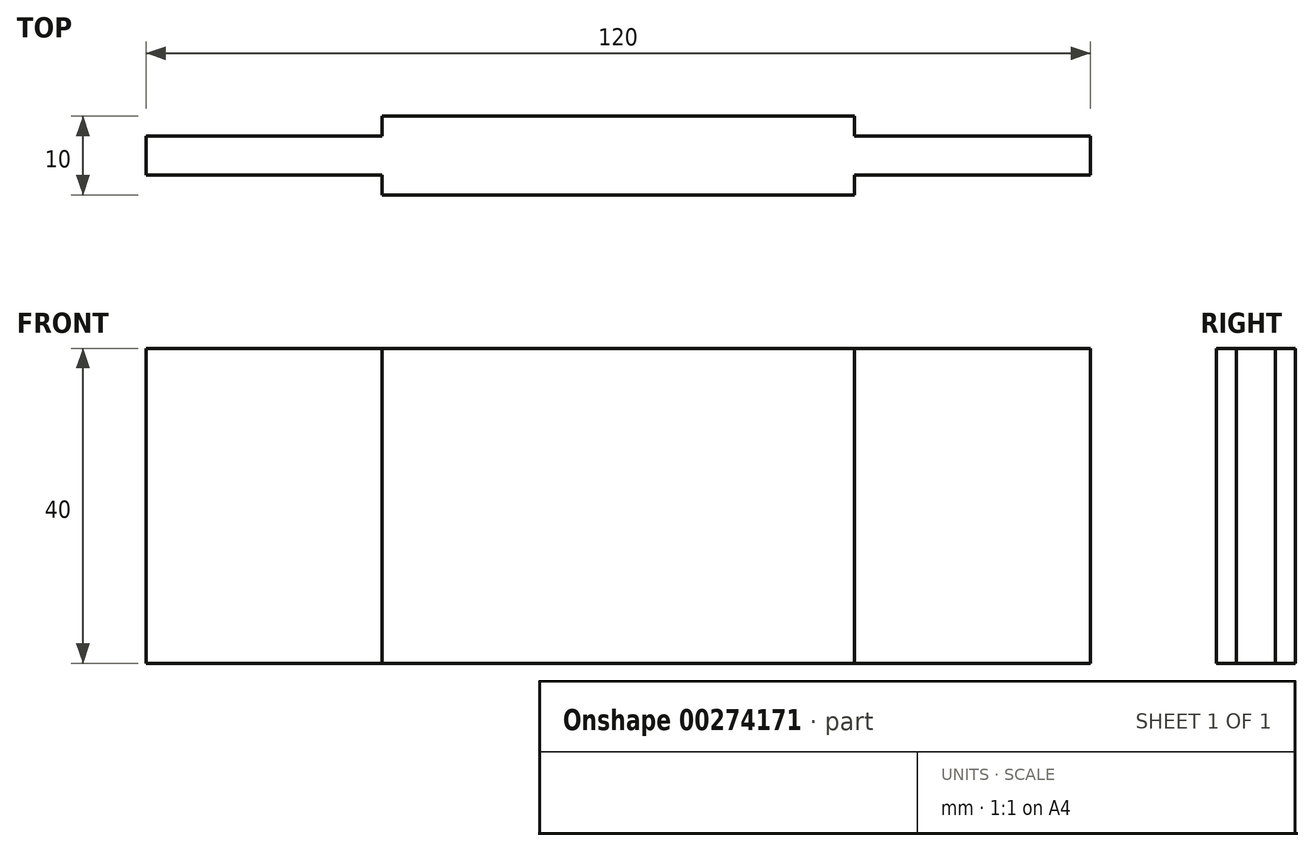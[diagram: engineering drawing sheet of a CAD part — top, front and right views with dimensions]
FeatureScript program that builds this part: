
annotation { "Feature Type Name" : "Feature", "Feature Type Description" : "" }
export const myFeature = defineFeature(function(context is Context, id is Id, definition is map)
    precondition{}
    {
        {
            var Q0;
            Q0=qCreatedBy(makeId("Top.planeOp"),FACE);
            var sketch = newSketch(context, id + "F0", { "sketchPlane" : qUnion([Q0])});
            skLineSegment(sketch, "E0.bottom", {"start": v(60, -5) * mm, "end": v(-60, -5) * mm});
            skLineSegment(sketch, "E0.top", {"start": v(60, 5) * mm, "end": v(-60, 5) * mm});
            skLineSegment(sketch, "E0.left", {"start": v(60, -5) * mm, "end": v(60, 5) * mm});
            skLineSegment(sketch, "E0.right", {"start": v(-60, -5) * mm, "end": v(-60, 5) * mm});
            skPoint(sketch, "E0.middle", {"position": v(0, 0) * mm});
            skLineSegment(sketch, "E1.bottom", {"start": v(-60, 5) * mm, "end": v(-30, 5) * mm});
            skLineSegment(sketch, "E1.top", {"start": v(-60, 2.5) * mm, "end": v(-30, 2.5) * mm});
            skLineSegment(sketch, "E1.left", {"start": v(-60, 5) * mm, "end": v(-60, 2.5) * mm});
            skLineSegment(sketch, "E1.right", {"start": v(-30, 5) * mm, "end": v(-30, 2.5) * mm});
            skLineSegment(sketch, "E2.MirrorCS", {"start": v(-60, -2.5) * mm, "end": v(-30, -2.5) * mm});
            skLineSegment(sketch, "E3.MirrorCS", {"start": v(-30, -5) * mm, "end": v(-30, -2.5) * mm});
            skLineSegment(sketch, "E4.MirrorCS", {"start": v(60, 2.5) * mm, "end": v(30, 2.5) * mm});
            skLineSegment(sketch, "E5.MirrorCS", {"start": v(30, 5) * mm, "end": v(30, 2.5) * mm});
            skLineSegment(sketch, "E6.MirrorCS", {"start": v(30, -5) * mm, "end": v(30, -2.5) * mm});
            skLineSegment(sketch, "E7.MirrorCS", {"start": v(60, -2.5) * mm, "end": v(30, -2.5) * mm});
            skSolve(sketch);
        }
        {
            var Q0;
            {var subQ4=sQuery(id+"F0.wireOp",EDGE,"E2.MirrorCS");Q0=makeQuery(id+"F0.imprint","IMPRINT",FACE,{"disambiguationData":[TD([[makeQuery(id+"F0.imprint","IMPRINT",EDGE,{"derivedFrom":subQ4}),1.0]])]});}
            extrude(context, id + "F1", {"entities" : qUnion([Q0]), "depth" : 40 * mm});
        }
    });
